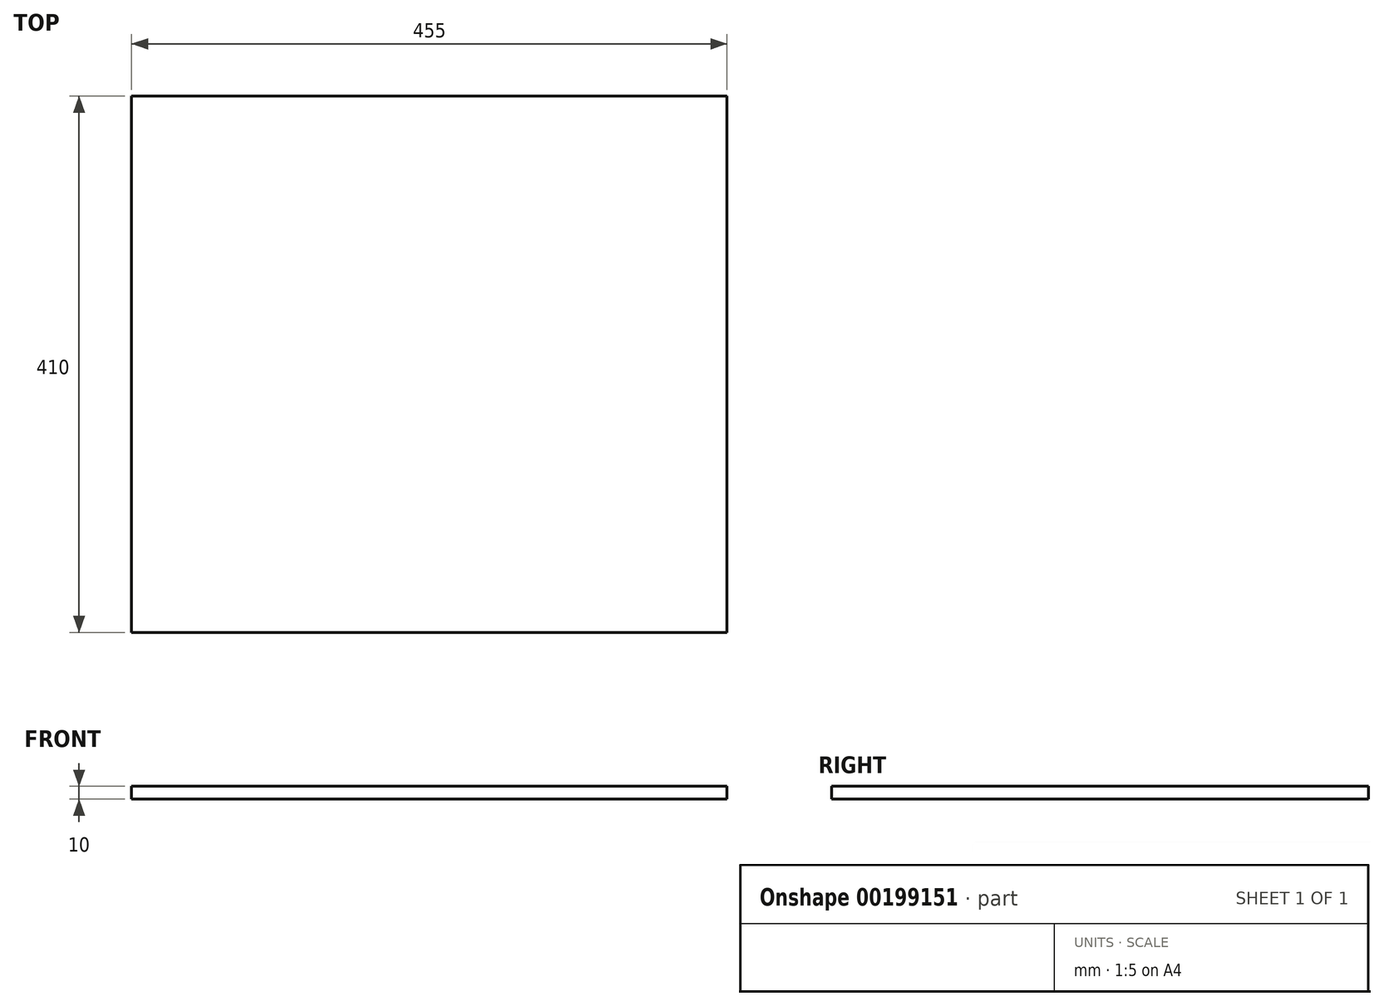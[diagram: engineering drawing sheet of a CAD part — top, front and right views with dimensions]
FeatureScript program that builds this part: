
annotation { "Feature Type Name" : "Feature", "Feature Type Description" : "" }
export const myFeature = defineFeature(function(context is Context, id is Id, definition is map)
    precondition{}
    {
        {
            var Q0;
            Q0=qCreatedBy(makeId("Top.planeOp"),FACE);
            var sketch = newSketch(context, id + "F0", { "sketchPlane" : qUnion([Q0])});
            skLineSegment(sketch, "E0.bottom", {"start": v(-70.96, 65.05) * mm, "end": v(384.04, 65.05) * mm});
            skLineSegment(sketch, "E0.top", {"start": v(-70.96, -344.95) * mm, "end": v(384.04, -344.95) * mm});
            skLineSegment(sketch, "E0.left", {"start": v(-70.96, 65.05) * mm, "end": v(-70.96, -344.95) * mm});
            skLineSegment(sketch, "E0.right", {"start": v(384.04, 65.05) * mm, "end": v(384.04, -344.95) * mm});
            skSolve(sketch);
        }
        {
            var Q0;
            Q0=qSketchRegion(id+"F0",true);
            extrude(context, id + "F1", {"entities" : qUnion([Q0]), "depth" : 10 * mm});
        }
    });
